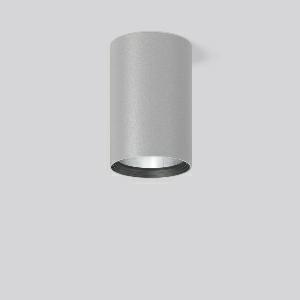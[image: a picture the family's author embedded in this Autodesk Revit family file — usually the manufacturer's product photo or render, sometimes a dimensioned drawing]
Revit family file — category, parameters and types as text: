
# Revit family: heledon_maxi_a_931218_004_2_4c0f
name_source: partatom
category: Lighting Fixtures
units: mm (PartAtom-declared; Revit-internal decimal feet)

## family parameters
Cut with Voids When Loaded = No
Host = Face
Light Source = No
Part Type = Normal
Room Calculation Point = No
Round Connector Dimension = Use Diameter
Shared = No

## types (1)
- HELEDON maxi A (1 x LED Modul 927, 3150 lm, 2700)
    Apparent Load = 25 VA
    Approval mark = CE
    CIE Flux Codes = 100 100 100 100 100
    Color Rendering = 92
    Color Temperature = 2700
    Default Elevation = 1800 mm
    Description = Series: HELEDON maxi
Cylindrical surface-mounted downlight. Housing: die-cast aluminium, powder-coated. Internal ceiling frame polycarbonate with bayonet mounting. Black plastic ring and recessed LED to prevent glare from the side. Optical assembly with reflector made of MIRO-Silver with 98% total light reflection for outstanding efficiency - can be changed without tools. Best colour rendering index Ra>90. Suitable for Ceiling mounting. Easy installation with a separate ceiling frame with bayonet mounting and plug connection. Driver integrated. Connected via plug-in connector. High quality converter without flickering and stroboscopic effect. The following accessories can be mounted without use of tools: interchangeable lenses, decorative glasses, honeycomb louvre, clear and frosted diffusers, white interchangeable plastic ring. 
Colour: silver
Diameter: 123 mm
Height: 183 mm
Lamp: LED
Socket: without socket
Colour temperature: 2700K
Colour rendering index (CRI): 92
System power: 25 W
Rated luminous flux: 3150 lm
Luminous efficiency: 126 lm/W
Control gear: Regulated power supply
Protection class: I
Type of protection: IP 20
    Height = 183 mm
    Lamp = 1 x LED Modul 927
    Lamp Light Flux = 3150 lm
    Lamp count = 1
    Length = 123 mm
    Lifetime = 50000 h
    Luminous efficacy = 126 lm/W
    Manufacturer = RZB
    ModVariant = No
    Model = 931218.004.2
    Mounting Place = Ceiling
    Mounting Type = Surface mounted
    Number of Poles = 1
    OnlyDefault = Yes
    Power Factor = 1
    Product Name = HELEDON maxi A
    Product group = Surface mounted downlights
    ProductGroupID = 302
    Protection Class = Protection class I
    Protection Degree = IP 20
    RLX_Detail_Level = 1
    RLX_Emergency_Light_Flux = 0 lm
    RLX_Emergency_Type = 0
    RLX_Emergency_Type_DB = No
    RlxData = <blob elided: 98089 chars, md5=35144f65>
    Socket = socket
    Standby Power = 0 W
    System Light Flux = 3150 lm
    System Power = 25 W
    Type Comments = Product without accessories
    Type Image = 931192.004.jpg
    URL = http://relux.com
    VarID = ---
    Voltage = 230 V
    Voltage Range = 220-240 V
    Weight = 0.00 kg
    Width = 0 mm  [stored 0 ft]

note: [stored X ft] marks values corroborated as IEEE doubles in the binary element streams (Revit-internal decimal feet)

## geometry (parser evidence)
native form markers: Blend x4, Sweep x10
no freeform markers — native parametric forms only
